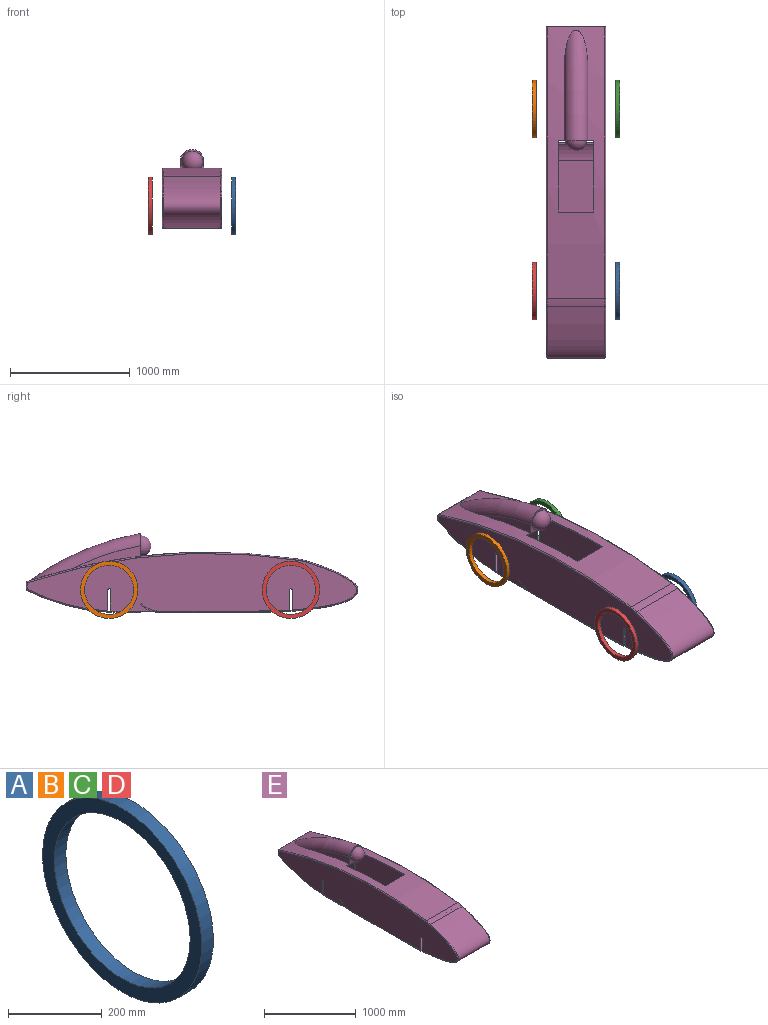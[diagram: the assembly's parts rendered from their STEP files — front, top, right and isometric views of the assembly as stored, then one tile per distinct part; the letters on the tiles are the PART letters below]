
ASSEMBLY  parts=5 mates=4
PART A: 4 faces, bbox 35x480x480 mm
  f0: cylinder r=205mm len=410mm, axis (-1,0,0), area 45081.9mm2, adj f2,f3
  f1: cylinder r=240mm len=480mm, axis (-1,0,0), area 52778.8mm2, adj f2,f3
  f2: plane 480x480mm, normal (1,0,0), area 48930.3mm2, adj f0,f1
  f3: plane 480x480mm, normal (-1,0,0), area 48930.3mm2, adj f0,f1
PART B: same geometry as A
PART C: same geometry as A
PART D: same geometry as A
PART E: 72 faces, bbox 536.8x3101.3x1076.3 mm
  f0: plane 235.4x53.12mm, normal (0,1,0), area 11571.4mm2, adj f52,f64,f67,f70
  f1: plane 244.4x53.12mm, normal (0,-1,0), area 12049.5mm2, adj f5,f10,f12,f64
  f2: cylinder r=257.9mm len=498mm, axis (-1,0,0), area 87154.1mm2, adj f3,f4,f12,f18,f38,f41,f56,f58
  f3: plane 99x7.46mm, normal (0,0.75,0.67), area 990mm2, adj f2,f7,f41,f60
  f4: plane 99x7.46mm, normal (0,0.75,0.67), area 990mm2, adj f2,f7,f12,f59
  f5: cylinder r=4818.85mm len=2299.4mm, axis (-1,0,0), area 979547.8mm2, adj f1,f9,f12,f13,f22,f41,f61,f62
  f6: cylinder r=4828.85mm len=2269.98mm, axis (-1,0,0), area 749560.5mm2, adj f16,f22,f23,f32,f35,f42,f53,f61
  f7: cylinder r=247.9mm len=498mm, axis (-1,0,0), area 81007.6mm2, adj f3,f4,f12,f19,f41,f58,f59,f60
  f8: plane 480x175mm, normal (0,0,-1), area 83998.2mm2, adj f15,f20,f38,f56
  f9: extruded ~915.1x498mm, area 746273.5mm2, adj f5,f12,f19,f29,f30,f31,f41,f48
  f10: cylinder r=1689.44mm len=769.43mm, axis (-1,0,0), area 396873.6mm2, adj f1,f12,f13,f14,f25,f26,f27,f41
  f11: plane 2752.56x484.49mm, normal (1,0,0), area 1043496mm2, adj f24,f25,f26,f28,f29,f30,f33,f34
  f12: plane 2935.84x488.85mm, normal (-1,0,0), area 1042609.9mm2, adj f1,f2,f4,f5,f7,f9,f10,f14
  f13: plane 244.4x53.12mm, normal (0,-1,0), area 12049.5mm2, adj f5,f10,f41,f64
  f14: plane 498x153.74mm, normal (0,0,1), area 76563.1mm2, adj f10,f12,f15,f41
  f15: cylinder r=27.59mm len=498mm, axis (-1,0,0), area 11922mm2, adj f8,f12,f14,f38,f41,f56
  f16: cylinder r=500mm len=480mm, axis (-1,0,0), area 34222mm2, adj f6,f17,f36,f54
  f17: extruded ~738.52x499.8mm, area 626778.1mm2, adj f16,f18,f29,f30,f31,f37,f38,f48
  f18: plane 908.66x480mm, normal (0,0,-1), area 436158.4mm2, adj f2,f17,f38,f56
  f19: plane 722.37x498mm, normal (0,0,1), area 359741.3mm2, adj f7,f9,f12,f41
  f20: cylinder r=1699.44mm len=773.98mm, axis (-1,0,0), area 385124.2mm2, adj f8,f25,f26,f27,f33,f39,f44,f45
  f21: plane 235.4x53.12mm, normal (0,1,0), area 11571.4mm2, adj f34,f64,f67,f70
  f22: plane 336.8x236.8mm, normal (0,-1,0), area 11201.6mm2, adj f5,f6,f23,f32,f42,f62,f63,f65
  f23: plane 565.37x190.62mm, normal (1,0,0), area 30204mm2, adj f6,f22,f32
  f24: cylinder r=10mm len=20mm, axis (1,0,0), area 31.4mm2, adj f11,f12,f25,f26
  f25: plane 187.58x25.24mm, normal (0,-1,0), area 406.2mm2, adj f10,f11,f12,f20,f24,f27,f33
  f26: plane 188.53x25.19mm, normal (0,1,0), area 407.1mm2, adj f10,f11,f12,f20,f24,f27,f39
  f27: plane 20x11.02mm, normal (1,0,0), area 200.3mm2, adj f10,f20,f25,f26
  f28: cylinder r=10mm len=20mm, axis (1,0,0), area 31.4mm2, adj f11,f12,f29,f30
  f29: plane 181.43x25mm, normal (0,-1,0), area 451.8mm2, adj f9,f11,f12,f17,f28,f31,f38
  f30: plane 180.43x25.43mm, normal (0,1,0), area 425.4mm2, adj f9,f11,f12,f17,f28,f31,f37
  f31: plane 20.02x12.56mm, normal (1,0,0), area 223.9mm2, adj f9,f17,f29,f30
  f32: torus R=2092.05mm, axis (1,0,0), area 268543.6mm2, adj f6,f22,f23,f42
  f33: torus R=1689.44mm, axis (1,0,0), area 11101.5mm2, adj f11,f20,f25,f71
  f34: cylinder r=10mm len=53.12mm, axis (0,0,-1), area 834.4mm2, adj f11,f21,f68,f71
  f35: torus R=4818.85mm, axis (1,0,0), area 36092.5mm2, adj f6,f11,f36,f68
  f36: torus R=490mm, axis (1,0,0), area 1111.8mm2, adj f11,f16,f35,f37
  f37: bspline ~881.5x562.02mm, area 17354.2mm2, adj f11,f17,f30,f36
  f38: cylinder r=10mm len=1423mm, axis (0,-1,0), area 19210.2mm2, adj f2,f8,f11,f12,f15,f17,f18,f29
  f39: torus R=1689.44mm, axis (1,0,0), area 1179.5mm2, adj f11,f20,f26,f38
  f40: plane 2752.56x484.49mm, normal (-1,0,0), area 1043496mm2, adj f43,f44,f45,f47,f48,f49,f51,f52
  f41: plane 2935.84x488.85mm, normal (1,0,0), area 1042609.9mm2, adj f2,f3,f5,f7,f9,f10,f13,f14
  f42: plane 565.37x190.62mm, normal (-1,0,0), area 30204mm2, adj f6,f22,f32
  f43: cylinder r=10mm len=20mm, axis (-1,0,0), area 31.4mm2, adj f40,f41,f44,f45
  f44: plane 187.58x25.24mm, normal (0,-1,0), area 406.2mm2, adj f10,f20,f40,f41,f43,f46,f51
  f45: plane 188.53x25.19mm, normal (0,1,0), area 407.1mm2, adj f10,f20,f40,f41,f43,f46,f57
  f46: plane 20x11.02mm, normal (-1,0,0), area 200.3mm2, adj f10,f20,f44,f45
  f47: cylinder r=10mm len=20mm, axis (-1,0,0), area 31.4mm2, adj f40,f41,f48,f49
  f48: plane 181.43x25mm, normal (0,-1,0), area 451.8mm2, adj f9,f17,f40,f41,f47,f50,f56
  f49: plane 180.43x25.43mm, normal (0,1,0), area 425.4mm2, adj f9,f17,f40,f41,f47,f50,f55
  f50: plane 20.02x12.56mm, normal (-1,0,0), area 223.9mm2, adj f9,f17,f48,f49
  f51: torus R=1689.44mm, axis (-1,0,0), area 11101.5mm2, adj f20,f40,f44,f69
  f52: cylinder r=10mm len=53.12mm, axis (0,0,-1), area 834.4mm2, adj f0,f40,f66,f69
  f53: torus R=4818.85mm, axis (-1,0,0), area 36092.5mm2, adj f6,f40,f54,f66
  f54: torus R=490mm, axis (-1,0,0), area 1111.8mm2, adj f16,f40,f53,f55
  f55: bspline ~881.5x562.02mm, area 17354.2mm2, adj f17,f40,f49,f54
  f56: cylinder r=10mm len=1423mm, axis (0,-1,0), area 19210.2mm2, adj f2,f8,f15,f17,f18,f40,f41,f48
  f57: torus R=1689.44mm, axis (-1,0,0), area 1179.5mm2, adj f20,f40,f45,f56
  f58: plane 300x16.97mm, normal (0,0,1), area 5091.1mm2, adj f2,f7,f59,f60
  f59: plane 31.22x19.29mm, normal (-1,0,0), area 248mm2, adj f2,f4,f7,f58
  f60: plane 31.22x19.29mm, normal (1,0,0), area 248mm2, adj f2,f3,f7,f58
  f61: plane 300x10mm, normal (0,1,0), area 3000mm2, adj f5,f6,f62,f63
  f62: plane 600x44.49mm, normal (1,0,0), area 6013.7mm2, adj f5,f6,f22,f61
  f63: plane 600x44.49mm, normal (-1,0,0), area 6013.7mm2, adj f5,f6,f22,f61
  f64: cylinder r=27.5mm len=55mm, axis (0,1,0), area 1727.9mm2, adj f0,f1,f5,f10,f13,f21,f67,f70
  f65: sphere r=90mm, area 50893.8mm2, adj f22
  f66: sphere r=10mm, area 86mm2, adj f52,f53,f67
  f67: cylinder r=10mm len=480mm, axis (-1,0,0), area 5981.6mm2, adj f0,f6,f21,f64,f66,f68
  f68: sphere r=10mm, area 86mm2, adj f34,f35,f67
  f69: sphere r=10mm, area 77.9mm2, adj f51,f52,f70
  f70: cylinder r=10mm len=480mm, axis (-1,0,0), area 5270.1mm2, adj f0,f20,f21,f64,f69,f71
  f71: sphere r=10mm, area 77.9mm2, adj f33,f34,f70
PLACE A t=(379.61,-754.06,261.36)mm
PLACE B t=(-315.39,763.94,261.36)mm
PLACE C t=(379.61,763.94,261.36)mm
PLACE D t=(-315.39,-754.06,261.36)mm
PLACE E t=(49.61,711.93,125.04)mm fixed
MATE fastened C.f0 <-> E.f24  axis (-1,0,0) through (379.61,763.94,261.36)mm
MATE fastened D.f0 <-> E.f28  axis (1,0,0) through (-280.39,-754.06,261.36)mm
MATE fastened B.f0 <-> E.f24  axis (1,0,0) through (-280.39,763.94,261.36)mm
MATE fastened A.f0 <-> E.f28  axis (-1,0,0) through (379.61,-754.06,261.36)mm
